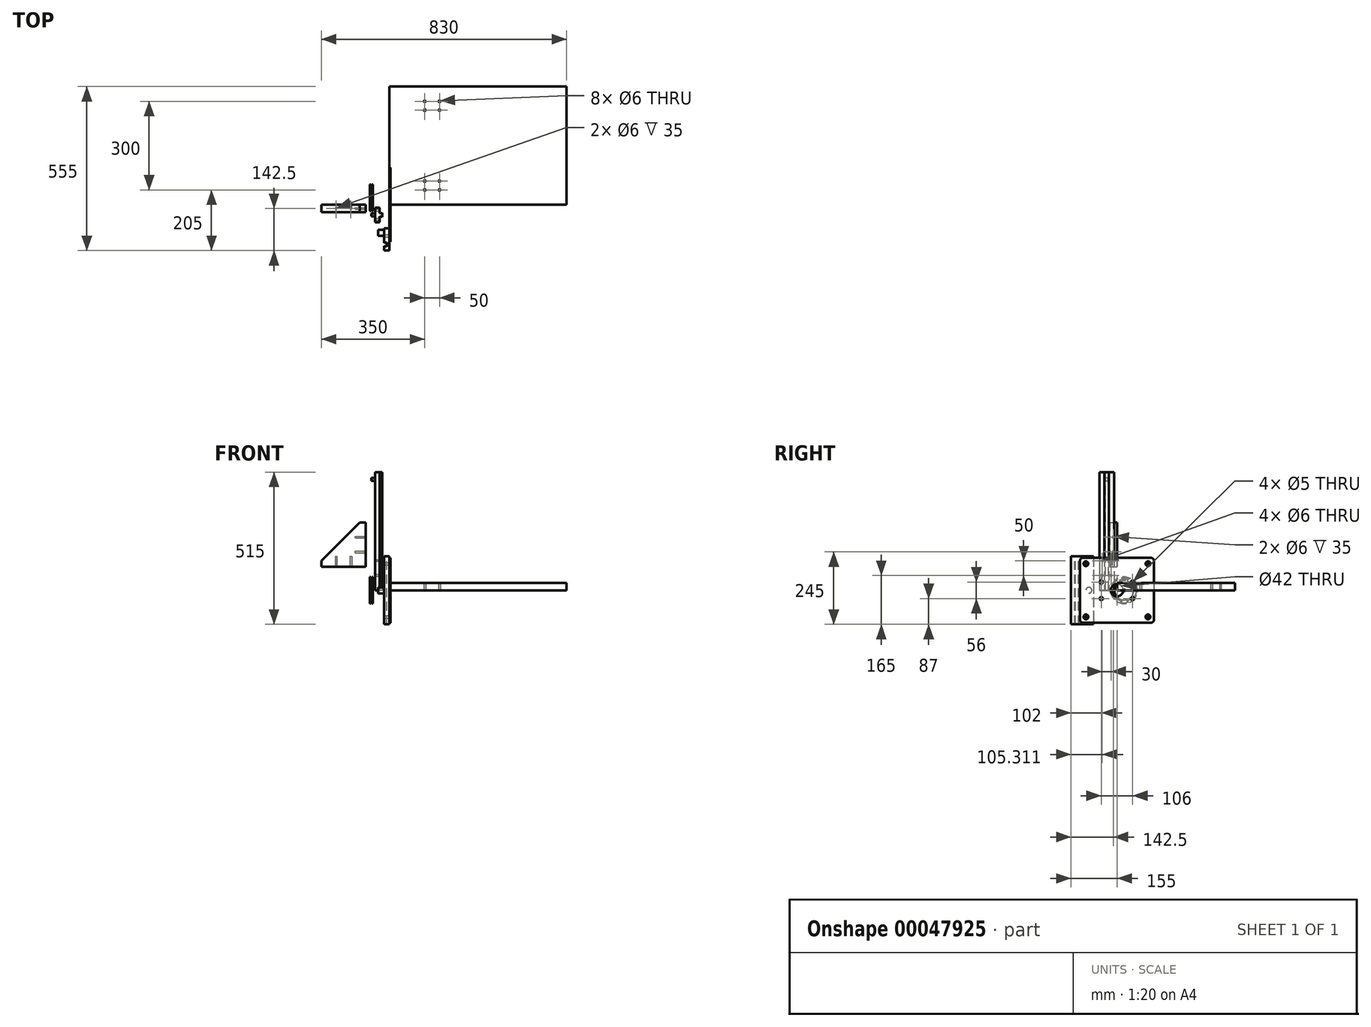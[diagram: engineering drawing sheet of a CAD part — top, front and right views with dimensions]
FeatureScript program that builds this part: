
annotation { "Feature Type Name" : "Feature", "Feature Type Description" : "" }
export const myFeature = defineFeature(function(context is Context, id is Id, definition is map)
    precondition{}
    {
        {
            var Q0;
            Q0=qCreatedBy(makeId("Right.planeOp"),FACE);
            var sketch = newSketch(context, id + "F0", { "sketchPlane" : qUnion([Q0])});
            skLineSegment(sketch, "E0.bottom", {"start": v(-115, 110) * mm, "end": v(115, 110) * mm});
            skLineSegment(sketch, "E0.top", {"start": v(-115, -110) * mm, "end": v(115, -110) * mm});
            skLineSegment(sketch, "E0.left", {"start": v(-125, 100) * mm, "end": v(-125, -100) * mm});
            skLineSegment(sketch, "E0.right", {"start": v(125, 100) * mm, "end": v(125, -100) * mm});
            skLineSegment(sketch, "E1", {"start": v(-125, 0) * mm, "end": v(125, 0) * mm, "construction": true});
            skLineSegment(sketch, "E2", {"start": v(0, 110) * mm, "end": v(0, -110) * mm, "construction": true});
            skCircle(sketch, "E3", {"center": v(0, 0) * mm, "radius": 21 * mm});
            skCircle(sketch, "E4", {"center": v(53, 28) * mm, "radius": 2.5 * mm});
            skCircle(sketch, "E5", {"center": v(53, -28) * mm, "radius": 2.5 * mm});
            skCircle(sketch, "E6", {"center": v(-53, -28) * mm, "radius": 2.5 * mm});
            skCircle(sketch, "E7", {"center": v(-53, 28) * mm, "radius": 2.5 * mm});
            skPoint(sketch, "E8.visualSharp", {"position": v(-125, 110) * mm});
            skArc(sketch, "E8.filletArc", {"start": v(-115, 110) * mm, "mid": v(-122.07, 107.07) * mm, "end": v(-125, 100) * mm});
            skPoint(sketch, "E9.visualSharp", {"position": v(125, 110) * mm});
            skArc(sketch, "E9.filletArc", {"start": v(125, 100) * mm, "mid": v(122.07, 107.07) * mm, "end": v(115, 110) * mm});
            skPoint(sketch, "E10.visualSharp", {"position": v(125, -110) * mm});
            skArc(sketch, "E10.filletArc", {"start": v(115, -110) * mm, "mid": v(122.07, -107.07) * mm, "end": v(125, -100) * mm});
            skPoint(sketch, "E11.visualSharp", {"position": v(-125, -110) * mm});
            skArc(sketch, "E11.filletArc", {"start": v(-125, -100) * mm, "mid": v(-122.07, -107.07) * mm, "end": v(-115, -110) * mm});
            skCircle(sketch, "E12", {"center": v(-105, 90) * mm, "radius": 4.12 * mm});
            skCircle(sketch, "E13", {"center": v(105, 90) * mm, "radius": 4.12 * mm});
            skCircle(sketch, "E14", {"center": v(105, -90) * mm, "radius": 4.12 * mm});
            skCircle(sketch, "E15", {"center": v(-105, -90) * mm, "radius": 4.12 * mm});
            skSolve(sketch);
        }
        {
            var Q0;
            Q0=makeQuery(id+"F0.imprint","IMPRINT",FACE,{"disambiguationData":[TD([[makeQuery(id+"F0.imprint","IMPRINT",EDGE,{"derivedFrom":sQuery(id+"F0.wireOp",EDGE,"E0.bottom")}),-1.0]])]});
            extrude(context, id + "F1", {"entities" : qUnion([Q0]), "depth" : 4 * mm});
        }
        {
            var Q0;
            Q0=makeQuery(id+"F1.opExtrude","CAP_EDGE",EDGE,{"disambiguationData":[OSD([sQuery(id+"F0.wireOp",EDGE,"E12")])],"isStart":false});
            var Q1;
            Q1=makeQuery(id+"F1.opExtrude","CAP_EDGE",EDGE,{"disambiguationData":[OSD([sQuery(id+"F0.wireOp",EDGE,"E13")])],"isStart":false});
            var Q2;
            Q2=makeQuery(id+"F1.opExtrude","CAP_EDGE",EDGE,{"disambiguationData":[OSD([sQuery(id+"F0.wireOp",EDGE,"E14")])],"isStart":false});
            var Q3;
            Q3=makeQuery(id+"F1.opExtrude","CAP_EDGE",EDGE,{"disambiguationData":[OSD([sQuery(id+"F0.wireOp",EDGE,"E15")])],"isStart":false});
            chamfer(context, id + "F2", {"entities" : qUnion([Q0, Q1, Q2, Q3]), "width" : 4 * mm});
        }
        {
            var Q0;
            Q0=makeQuery(id+"F1.opExtrude","CAP_EDGE",EDGE,{"disambiguationData":[OSD([sQuery(id+"F0.wireOp",EDGE,"E7")])],"isStart":false});
            var Q1;
            Q1=makeQuery(id+"F1.opExtrude","CAP_EDGE",EDGE,{"disambiguationData":[OSD([sQuery(id+"F0.wireOp",EDGE,"E6")])],"isStart":false});
            var Q2;
            Q2=makeQuery(id+"F1.opExtrude","CAP_EDGE",EDGE,{"disambiguationData":[OSD([sQuery(id+"F0.wireOp",EDGE,"E5")])],"isStart":false});
            var Q3;
            Q3=makeQuery(id+"F1.opExtrude","CAP_EDGE",EDGE,{"disambiguationData":[OSD([sQuery(id+"F0.wireOp",EDGE,"E4")])],"isStart":false});
            chamfer(context, id + "F3", {"entities" : qUnion([Q0, Q1, Q2, Q3]), "width" : 3 * mm});
        }
        {
            var Q0;
            Q0=makeQuery(id+"F1.opExtrude","CAP_FACE",FACE,{"disambiguationData":[OSD([sQuery(id+"F0.wireOp",EDGE,"E0.bottom"),sQuery(id+"F0.wireOp",EDGE,"E0.top"),sQuery(id+"F0.wireOp",EDGE,"E0.left"),sQuery(id+"F0.wireOp",EDGE,"E0.right"),sQuery(id+"F0.wireOp",EDGE,"E3"),sQuery(id+"F0.wireOp",EDGE,"E4"),sQuery(id+"F0.wireOp",EDGE,"E5"),sQuery(id+"F0.wireOp",EDGE,"E6"),sQuery(id+"F0.wireOp",EDGE,"E7"),sQuery(id+"F0.wireOp",EDGE,"E8.filletArc"),sQuery(id+"F0.wireOp",EDGE,"E9.filletArc"),sQuery(id+"F0.wireOp",EDGE,"E10.filletArc"),sQuery(id+"F0.wireOp",EDGE,"E11.filletArc"),sQuery(id+"F0.wireOp",EDGE,"E12"),sQuery(id+"F0.wireOp",EDGE,"E13"),sQuery(id+"F0.wireOp",EDGE,"E14"),sQuery(id+"F0.wireOp",EDGE,"E15")])],"isStart":true});
            var sketch = newSketch(context, id + "F4", { "sketchPlane" : qUnion([Q0])});
            skLineSegment(sketch, "E16.bottom", {"start": v(80, 115) * mm, "end": v(155, 115) * mm});
            skLineSegment(sketch, "E16.top", {"start": v(80, -115) * mm, "end": v(155, -115) * mm});
            skLineSegment(sketch, "E16.left", {"start": v(80, 115) * mm, "end": v(80, -115) * mm});
            skLineSegment(sketch, "E16.right", {"start": v(155, 115) * mm, "end": v(155, -115) * mm});
            skLineSegment(sketch, "E17", {"start": v(105, 115) * mm, "end": v(105, -115) * mm, "construction": true});
            skCircle(sketch, "E18.0", {"center": v(105, 90) * mm, "radius": 4.12 * mm});
            skCircle(sketch, "E19.0", {"center": v(105, -90) * mm, "radius": 4.12 * mm});
            skSolve(sketch);
        }
        {
            var Q0;
            Q0 = qSketchRegion(id + "F4", true);
            extrude(context, id + "F5", {"entities" : qUnion([Q0]), "depth" : 18 * mm});
        }
        {
            var Q0;
            Q0=makeQuery(id+"F5.opExtrude","SWEPT_FACE",FACE,{"disambiguationData":[OSD([sQuery(id+"F4.wireOp",EDGE,"E16.bottom")])]});
            var sketch = newSketch(context, id + "F6", { "sketchPlane" : qUnion([Q0])});
            skLineSegment(sketch, "E20", {"start": v(-18, -140.01) * mm, "end": v(-8, -142.5) * mm});
            skLineSegment(sketch, "E21", {"start": v(-8, -142.5) * mm, "end": v(-8, -127.5) * mm});
            skLineSegment(sketch, "E22", {"start": v(-8, -127.5) * mm, "end": v(-18, -130) * mm});
            skLineSegment(sketch, "E23", {"start": v(-18, -130) * mm, "end": v(-18, -140.01) * mm});
            skSolve(sketch);
        }
        {
            var Q0;
            Q0 = qSketchRegion(id + "F6", true);
            var Q1;
            Q1=makeQuery(id+"F5.opExtrude","SWEPT_FACE",FACE,{"disambiguationData":[OSD([sQuery(id+"F4.wireOp",EDGE,"E16.top")])]});
            extrude(context, id + "F7", {"entities" : qUnion([Q0]), "operationType" : NewBodyOperationType.REMOVE, "endBound" : BoundingType.UP_TO_SURFACE, "oppositeDirection" : true, "endBoundEntityFace" : qUnion([Q1]), "depth" : 25 * mm});
        }
        {
            var Q0;
            {var subQ0=sQuery(id+"F4.wireOp",EDGE,"E18.0");var subQ1=sQuery(id+"F4.wireOp",EDGE,"E16.top");var subQ2=sQuery(id+"F4.wireOp",EDGE,"E16.left");var subQ3=sQuery(id+"F4.wireOp",EDGE,"E16.bottom");var subQ4=sQuery(id+"F4.wireOp",EDGE,"E19.0");Q0=makeQuery(id+"F7.boolean.opBoolean","SPLIT",FACE,{"disambiguationData":[TD([makeQuery(id+"F5.opExtrude","SWEPT_FACE",FACE,{"disambiguationData":[OSD([subQ2])]})])],"derivedFrom":makeQuery(id+"F5.opExtrude","CAP_FACE",FACE,{"disambiguationData":[OSD([subQ3,subQ1,subQ2,sQuery(id+"F4.wireOp",EDGE,"E16.right"),subQ0,subQ4])],"isStart":false})});}
            var sketch = newSketch(context, id + "F8", { "sketchPlane" : qUnion([Q0])});
            skCircle(sketch, "E24", {"center": v(95, 0) * mm, "radius": 10 * mm});
            skSolve(sketch);
        }
        {
            var Q0;
            Q0 = qSketchRegion(id + "F8", true);
            extrude(context, id + "F9", {"entities" : qUnion([Q0]), "operationType" : NewBodyOperationType.ADD, "depth" : 20 * mm});
        }
        {
            var Q0;
            Q0=qCreatedBy(makeId("Top.planeOp"),FACE);
            var sketch = newSketch(context, id + "F10", { "sketchPlane" : qUnion([Q0])});
            skLineSegment(sketch, "E25", {"start": v(-32.6, -59.69) * mm, "end": v(-48.6, -59.69) * mm});
            skLineSegment(sketch, "E26", {"start": v(-48.6, -59.69) * mm, "end": v(-48.6, -9.69) * mm});
            skLineSegment(sketch, "E27", {"start": v(-48.6, -9.69) * mm, "end": v(-32.6, -9.69) * mm});
            skLineSegment(sketch, "E28", {"start": v(-32.6, -9.69) * mm, "end": v(-32.6, -29.69) * mm});
            skLineSegment(sketch, "E29", {"start": v(-32.6, -29.69) * mm, "end": v(-23.6, -27.45) * mm});
            skLineSegment(sketch, "E30", {"start": v(-23.6, -27.45) * mm, "end": v(-23.6, -41.93) * mm});
            skLineSegment(sketch, "E31", {"start": v(-23.6, -41.93) * mm, "end": v(-32.6, -39.69) * mm});
            skLineSegment(sketch, "E32", {"start": v(-32.6, -39.69) * mm, "end": v(-32.6, -59.69) * mm});
            skSolve(sketch);
        }
        {
            var Q0;
            Q0 = qSketchRegion(id + "F10", true);
            extrude(context, id + "F11", {"entities" : qUnion([Q0]), "depth" : 400 * mm});
        }
        {
            var Q0;
            Q0=makeQuery(id+"F11.opExtrude","SWEPT_FACE",FACE,{"disambiguationData":[OSD([sQuery(id+"F10.wireOp",EDGE,"E26")])]});
            var sketch = newSketch(context, id + "F12", { "sketchPlane" : qUnion([Q0])});
            skCircle(sketch, "E33", {"center": v(49.69, 50) * mm, "radius": 3 * mm});
            skCircle(sketch, "E34", {"center": v(49.69, 100) * mm, "radius": 3 * mm});
            skCircle(sketch, "E35", {"center": v(19.69, 100) * mm, "radius": 3 * mm});
            skCircle(sketch, "E36", {"center": v(19.69, 50) * mm, "radius": 3 * mm});
            skSolve(sketch);
        }
        {
            var Q0;
            Q0 = qSketchRegion(id + "F12", true);
            extrude(context, id + "F13", {"entities" : qUnion([Q0]), "operationType" : NewBodyOperationType.REMOVE, "oppositeDirection" : true, "depth" : 25 * mm});
        }
        {
            var Q0;
            Q0=makeQuery(id+"F11.opExtrude","SWEPT_FACE",FACE,{"disambiguationData":[OSD([sQuery(id+"F10.wireOp",EDGE,"E26")])]});
            var sketch = newSketch(context, id + "F14", { "sketchPlane" : qUnion([Q0])});
            skCircle(sketch, "E37", {"center": v(34.69, 375) * mm, "radius": 5 * mm});
            skPoint(sketch, "E37.centerSnap0", {"position": v(34.69, 400) * mm});
            skSolve(sketch);
        }
        {
            var Q0;
            Q0 = qSketchRegion(id + "F14", true);
            extrude(context, id + "F15", {"entities" : qUnion([Q0]), "operationType" : NewBodyOperationType.ADD, "depth" : 12 * mm});
        }
        {
            var Q0;
            Q0=qCreatedBy(makeId("Top.planeOp"),FACE);
            var sketch = newSketch(context, id + "F16", { "sketchPlane" : qUnion([Q0])});
            skLineSegment(sketch, "E38", {"start": v(-62.58, 29.15) * mm, "end": v(-62.58, 57.15) * mm});
            skLineSegment(sketch, "E39", {"start": v(-62.58, 57.15) * mm, "end": v(-65.58, 61.15) * mm});
            skLineSegment(sketch, "E40", {"start": v(-65.58, 61.15) * mm, "end": v(-65.58, 69.15) * mm});
            skLineSegment(sketch, "E41", {"start": v(-65.58, 69.15) * mm, "end": v(-63.08, 69.15) * mm});
            skLineSegment(sketch, "E42", {"start": v(-63.08, 69.15) * mm, "end": v(-61.83, 66.15) * mm});
            skLineSegment(sketch, "E43", {"start": v(-61.83, 66.15) * mm, "end": v(-59.33, 66.15) * mm});
            skLineSegment(sketch, "E44", {"start": v(-59.33, 66.15) * mm, "end": v(-58.08, 69.15) * mm});
            skLineSegment(sketch, "E45", {"start": v(-58.08, 69.15) * mm, "end": v(-55.58, 69.15) * mm});
            skLineSegment(sketch, "E46", {"start": v(-55.58, 69.15) * mm, "end": v(-55.58, 61.15) * mm});
            skLineSegment(sketch, "E47", {"start": v(-55.58, 61.15) * mm, "end": v(-58.58, 57.15) * mm});
            skLineSegment(sketch, "E48", {"start": v(-58.58, 57.15) * mm, "end": v(-58.58, 29.15) * mm});
            skLineSegment(sketch, "E49", {"start": v(-58.58, 29.15) * mm, "end": v(-62.58, 29.15) * mm});
            skLineSegment(sketch, "E50", {"start": v(-65.58, 24.15) * mm, "end": v(-55.58, 24.15) * mm, "construction": true});
            skSolve(sketch);
        }
        {
            var Q0;
            Q0=makeQuery(id+"F16.imprint","IMPRINT",FACE,{"disambiguationData":[TD([[makeQuery(id+"F16.imprint","IMPRINT",EDGE,{"derivedFrom":sQuery(id+"F16.wireOp",EDGE,"E38")}),-1.0]])]});
            var Q1;
            Q1=sQuery(id+"F16.wireOp",EDGE,"E50");
            revolve(context, id + "F17", {"entities" : qUnion([Q0]), "axis" : qUnion([Q1]), "revolveType" : RevolveType.FULL});
        }
        {
            var Q0;
            Q0=qCreatedBy(makeId("Top.planeOp"),FACE);
            var sketch = newSketch(context, id + "F18", { "sketchPlane" : qUnion([Q0])});
            skLineSegment(sketch, "E51.bottom", {"start": v(0, 400) * mm, "end": v(600, 400) * mm});
            skLineSegment(sketch, "E51.top", {"start": v(0, 0) * mm, "end": v(600, 0) * mm});
            skLineSegment(sketch, "E51.left", {"start": v(0, 400) * mm, "end": v(0, 0) * mm});
            skLineSegment(sketch, "E51.right", {"start": v(600, 400) * mm, "end": v(600, 0) * mm});
            skCircle(sketch, "E52", {"center": v(120, 50) * mm, "radius": 3 * mm});
            skCircle(sketch, "E53", {"center": v(170, 50) * mm, "radius": 3 * mm});
            skCircle(sketch, "E54", {"center": v(120, 80) * mm, "radius": 3 * mm});
            skCircle(sketch, "E55", {"center": v(170, 80) * mm, "radius": 3 * mm});
            skCircle(sketch, "E56", {"center": v(120, 320) * mm, "radius": 3 * mm});
            skCircle(sketch, "E57", {"center": v(170, 320) * mm, "radius": 3 * mm});
            skCircle(sketch, "E58", {"center": v(120, 350) * mm, "radius": 3 * mm});
            skCircle(sketch, "E59", {"center": v(170, 350) * mm, "radius": 3 * mm});
            skSolve(sketch);
        }
        {
            var Q0;
            Q0=makeQuery(id+"F18.imprint","IMPRINT",FACE,{"disambiguationData":[TD([[makeQuery(id+"F18.imprint","IMPRINT",EDGE,{"derivedFrom":sQuery(id+"F18.wireOp",EDGE,"E51.bottom")}),-1.0]])]});
            extrude(context, id + "F19", {"entities" : qUnion([Q0]), "depth" : 25 * mm});
        }
        {
            var Q0;
            Q0=qCreatedBy(makeId("Front.planeOp"),FACE);
            var sketch = newSketch(context, id + "F20", { "sketchPlane" : qUnion([Q0])});
            skLineSegment(sketch, "E60", {"start": v(-80, 80) * mm, "end": v(-230, 80) * mm});
            skLineSegment(sketch, "E61", {"start": v(-80, 230) * mm, "end": v(-80, 80) * mm});
            skLineSegment(sketch, "E62", {"start": v(-230, 80) * mm, "end": v(-230, 100) * mm});
            skLineSegment(sketch, "E63", {"start": v(-230, 100) * mm, "end": v(-100, 230) * mm});
            skLineSegment(sketch, "E64", {"start": v(-100, 230) * mm, "end": v(-80, 230) * mm});
            skSolve(sketch);
        }
        {
            var Q0;
            Q0 = qSketchRegion(id + "F20", true);
            extrude(context, id + "F21", {"entities" : qUnion([Q0]), "depth" : 25 * mm});
        }
        {
            var Q0;
            Q0=makeQuery(id+"F21.opExtrude","SWEPT_FACE",FACE,{"disambiguationData":[OSD([sQuery(id+"F20.wireOp",EDGE,"E60")])]});
            var sketch = newSketch(context, id + "F22", { "sketchPlane" : qUnion([Q0])});
            skLineSegment(sketch, "E65", {"start": v(-80, 12.5) * mm, "end": v(-80, 12.5) * mm});
            skCircle(sketch, "E66", {"center": v(-180, 12.5) * mm, "radius": 3 * mm});
            skCircle(sketch, "E67", {"center": v(-130, 12.5) * mm, "radius": 3 * mm});
            skSolve(sketch);
        }
        {
            var Q0;
            Q0 = qSketchRegion(id + "F22", true);
            extrude(context, id + "F23", {"entities" : qUnion([Q0]), "operationType" : NewBodyOperationType.REMOVE, "oppositeDirection" : true, "depth" : 35 * mm});
        }
        {
            var Q0;
            Q0=makeQuery(id+"F21.opExtrude","SWEPT_FACE",FACE,{"disambiguationData":[OSD([sQuery(id+"F20.wireOp",EDGE,"E61")])]});
            var sketch = newSketch(context, id + "F24", { "sketchPlane" : qUnion([Q0])});
            skLineSegment(sketch, "E68", {"start": v(-12.5, 80) * mm, "end": v(-12.5, 80) * mm});
            skCircle(sketch, "E69", {"center": v(-12.5, 180) * mm, "radius": 3 * mm});
            skCircle(sketch, "E70", {"center": v(-12.5, 130) * mm, "radius": 3 * mm});
            skSolve(sketch);
        }
        {
            var Q0;
            Q0 = qSketchRegion(id + "F24", true);
            extrude(context, id + "F25", {"entities" : qUnion([Q0]), "operationType" : NewBodyOperationType.REMOVE, "oppositeDirection" : true, "depth" : 35 * mm});
        }
    });
